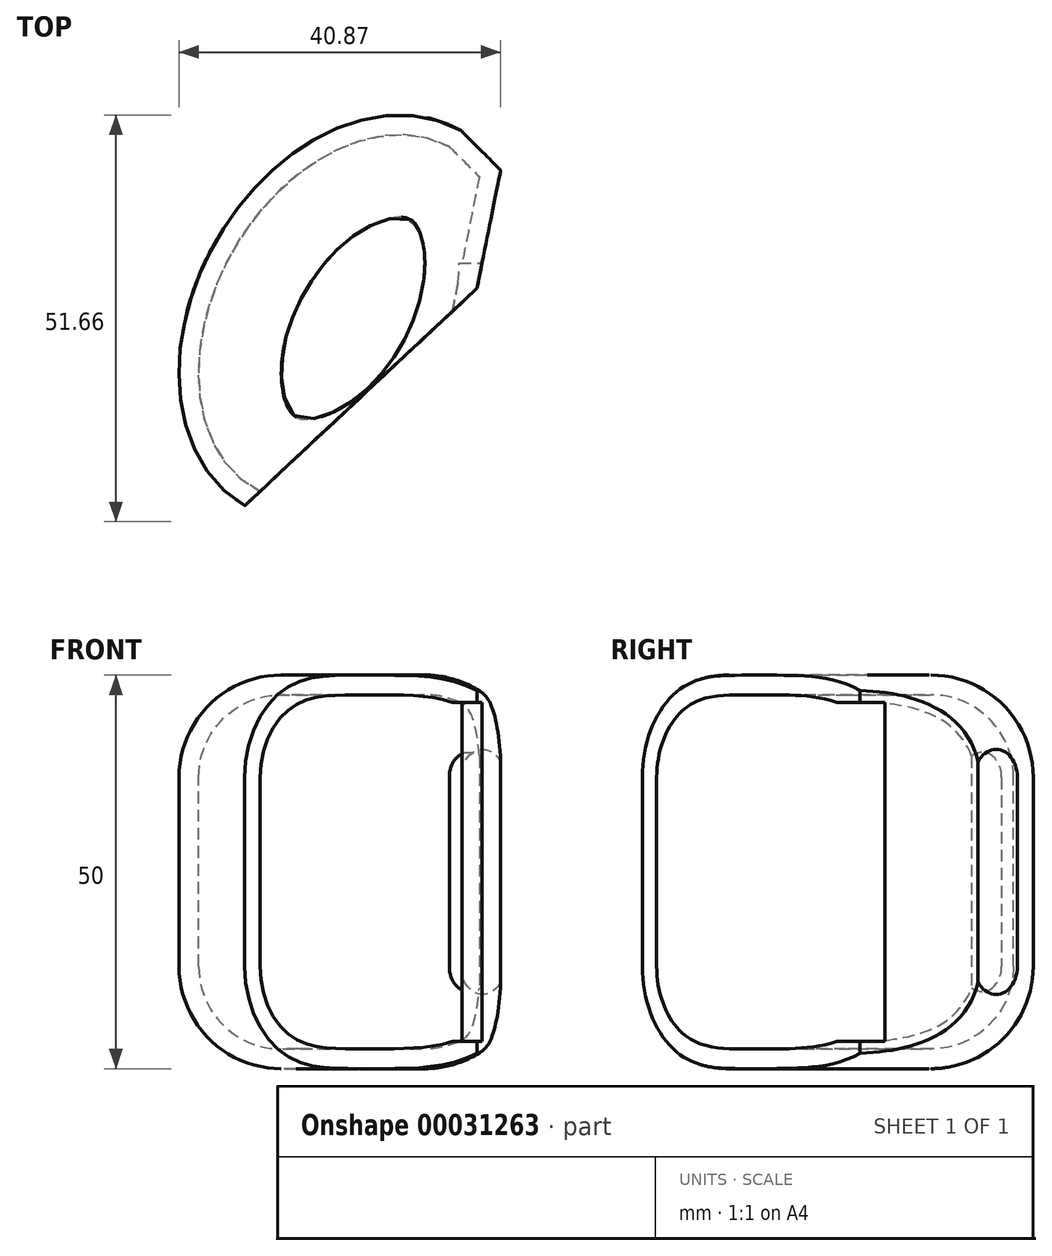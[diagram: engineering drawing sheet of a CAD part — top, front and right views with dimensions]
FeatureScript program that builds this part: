
annotation { "Feature Type Name" : "Feature", "Feature Type Description" : "" }
export const myFeature = defineFeature(function(context is Context, id is Id, definition is map)
    precondition{}
    {
        {
            var Q0;
            Q0=qCreatedBy(makeId("Top.planeOp"),FACE);
            var sketch = newSketch(context, id + "F0", { "sketchPlane" : qUnion([Q0])});
            skEllipticalArc(sketch, "E0", {});
            skPoint(sketch, "E1", {"position": v(13.75, 23.82) * mm});
            skPoint(sketch, "E2", {"position": v(-17.32, 10) * mm});
            skLineSegment(sketch, "E3", {"start": v(13.75, 23.82) * mm, "end": v(0, 0) * mm, "construction": true});
            skLineSegment(sketch, "E4", {"start": v(0, 0) * mm, "end": v(-13.75, -23.82) * mm, "construction": true});
            skLineSegment(sketch, "E5", {"start": v(13.75, 23.82) * mm, "end": v(18.75, 18.82) * mm});
            skLineSegment(sketch, "E6", {"start": v(18.75, 18.82) * mm, "end": v(15.75, 3.82) * mm});
            skLineSegment(sketch, "E7", {"start": v(15.75, 3.82) * mm, "end": v(-13.75, -23.82) * mm});
            const initialGuessF0  = {"E0": [0, 0, 0.5, 0.8660254037844386, 0.0275, 0.02, 0, 3.141592653589793]};
            skSetInitialGuess(sketch, initialGuessF0);
            skSolve(sketch);
        }
        {
            var Q0;
            Q0 = qSketchRegion(id + "F0", true);
            extrude(context, id + "F1", {"entities" : qUnion([Q0]), "depth" : 25 * mm, "hasSecondDirection" : true, "secondDirectionOppositeDirection" : true, "secondDirectionDepth" : 25 * mm});
        }
        {
            var Q0;
            Q0=makeQuery(id+"F1.opExtrude","CAP_EDGE",EDGE,{"disambiguationData":[OSD([sQuery(id+"F0.wireOp",EDGE,"E0")])],"isStart":true});
            var Q1;
            Q1=makeQuery(id+"F1.opExtrude","CAP_EDGE",EDGE,{"disambiguationData":[OSD([sQuery(id+"F0.wireOp",EDGE,"E0")])],"isStart":false});
            fillet(context, id + "F2", {"entities" : qUnion([Q0, Q1]), "radius" : 13 * mm, "tangentPropagation" : true, "allowEdgeOverflow" : false});
        }
        {
            var Q0;
            Q0=makeQuery(id+"F1.opExtrude","SWEPT_FACE",FACE,{"disambiguationData":[OSD([sQuery(id+"F0.wireOp",EDGE,"E7")])]});
            shell(context, id + "F3", {"entities" : qUnion([Q0]), "thickness" : 2.5 * mm});
        }
        {
            var Q0;
            Q0=qCreatedBy(makeId("Front.planeOp"),FACE);
            var sketch = newSketch(context, id + "F4", { "sketchPlane" : qUnion([Q0])});
            skLineSegment(sketch, "E8.bottom", {"start": v(12.61, 21.55) * mm, "end": v(17.61, 21.55) * mm});
            skLineSegment(sketch, "E8.top", {"start": v(12.61, -21.55) * mm, "end": v(17.61, -21.55) * mm});
            skLineSegment(sketch, "E8.left", {"start": v(12.61, 21.55) * mm, "end": v(12.61, -21.55) * mm});
            skLineSegment(sketch, "E8.right", {"start": v(17.61, 21.55) * mm, "end": v(17.61, -21.55) * mm});
            skPoint(sketch, "E8.middle", {"position": v(15.11, 0) * mm});
            skSolve(sketch);
        }
        {
            var Q0;
            Q0 = qSketchRegion(id + "F4", true);
            extrude(context, id + "F5", {"entities" : qUnion([Q0]), "operationType" : NewBodyOperationType.REMOVE, "oppositeDirection" : true, "depth" : 7 * mm, "hasSecondDirection" : true, "secondDirectionOppositeDirection" : false, "secondDirectionDepth" : 5 * mm});
        }
    });
